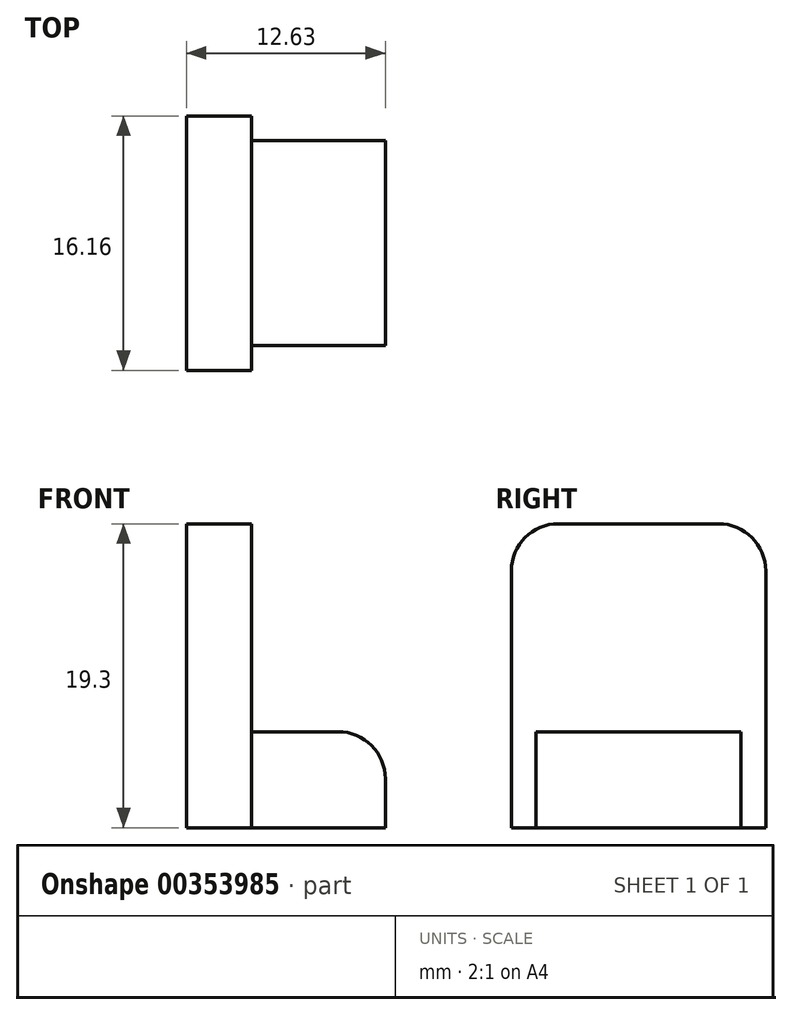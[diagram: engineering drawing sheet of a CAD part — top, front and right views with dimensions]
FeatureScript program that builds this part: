
annotation { "Feature Type Name" : "Feature", "Feature Type Description" : "" }
export const myFeature = defineFeature(function(context is Context, id is Id, definition is map)
    precondition{}
    {
        {
            var Q0;
            Q0=qCreatedBy(makeId("Top.planeOp"),FACE);
            var sketch = newSketch(context, id + "F0", { "sketchPlane" : qUnion([Q0])});
            skLineSegment(sketch, "E0", {"start": v(-6.1, 0) * mm, "end": v(-6.1, 8.08) * mm});
            skLineSegment(sketch, "E1", {"start": v(-6.1, 8.08) * mm, "end": v(-1.97, 8.08) * mm});
            skLineSegment(sketch, "E2", {"start": v(-1.97, 8.08) * mm, "end": v(-1.97, 6.5) * mm});
            skLineSegment(sketch, "E3.MirrorCS", {"start": v(-6.1, -8.08) * mm, "end": v(-1.97, -8.08) * mm});
            skLineSegment(sketch, "E4.MirrorCS", {"start": v(-6.1, 0) * mm, "end": v(-6.1, -8.08) * mm});
            skLineSegment(sketch, "E5.MirrorCS", {"start": v(-1.97, -8.08) * mm, "end": v(-1.97, -6.5) * mm});
            skLineSegment(sketch, "E6", {"start": v(-1.97, 6.5) * mm, "end": v(6.52, 6.5) * mm});
            skLineSegment(sketch, "E7", {"start": v(6.52, 6.5) * mm, "end": v(6.52, -6.5) * mm});
            skLineSegment(sketch, "E8", {"start": v(6.52, -6.5) * mm, "end": v(-1.97, -6.5) * mm});
            skLineSegment(sketch, "E9", {"start": v(-1.97, 6.5) * mm, "end": v(-1.97, -6.5) * mm});
            skLineSegment(sketch, "E10", {"start": v(2.28, 6.5) * mm, "end": v(2.28, -6.5) * mm});
            skSolve(sketch);
        }
        {
            var Q0;
            Q0=makeQuery(id+"F0.imprint","IMPRINT",FACE,{"disambiguationData":[TD([[makeQuery(id+"F0.imprint","IMPRINT",EDGE,{"derivedFrom":sQuery(id+"F0.wireOp",EDGE,"E0")}),-1.0]])]});
            extrude(context, id + "F1", {"entities" : qUnion([Q0]), "depth" : 19.3 * mm});
        }
        {
            var Q0;
            Q0=makeQuery(id+"F0.imprint","IMPRINT",FACE,{"disambiguationData":[TD([[makeQuery(id+"F0.imprint","IMPRINT",EDGE,{"derivedFrom":sQuery(id+"F0.wireOp",EDGE,"E6")}),-1.0]])]});
            extrude(context, id + "F2", {"entities" : qUnion([Q0]), "operationType" : NewBodyOperationType.ADD, "depth" : 6.1 * mm});
        }
        {
            var Q0;
            Q0=makeQuery(id+"F1.opExtrude","CAP_EDGE",EDGE,{"disambiguationData":[OSD([sQuery(id+"F0.wireOp",EDGE,"E3.MirrorCS")])],"isStart":false});
            var Q1;
            Q1=makeQuery(id+"F1.opExtrude","CAP_EDGE",EDGE,{"disambiguationData":[OSD([sQuery(id+"F0.wireOp",EDGE,"E1")])],"isStart":false});
            var Q2;
            Q2=makeQuery(id+"F2.opExtrude","SWEPT_EDGE",EDGE,{"disambiguationData":[OSD([sQuery(id+"F0.wireOp",EDGE,"E5.MirrorCS"),sQuery(id+"F0.wireOp",EDGE,"E8"),sQuery(id+"F0.wireOp",EDGE,"E9")])]});
            var Q3;
            Q3=makeQuery(id+"F2.opExtrude","SWEPT_EDGE",EDGE,{"disambiguationData":[OSD([sQuery(id+"F0.wireOp",EDGE,"E2"),sQuery(id+"F0.wireOp",EDGE,"E6"),sQuery(id+"F0.wireOp",EDGE,"E9")])]});
            var Q4;
            Q4=makeQuery(id+"F2.opExtrude","CAP_EDGE",EDGE,{"disambiguationData":[OSD([sQuery(id+"F0.wireOp",EDGE,"E7")])],"isStart":false});
            fillet(context, id + "F3", {"entities" : qUnion([Q0, Q1, Q2, Q3, Q4]), "radius" : 3 * mm, "tangentPropagation" : true, "allowEdgeOverflow" : false});
        }
    });
